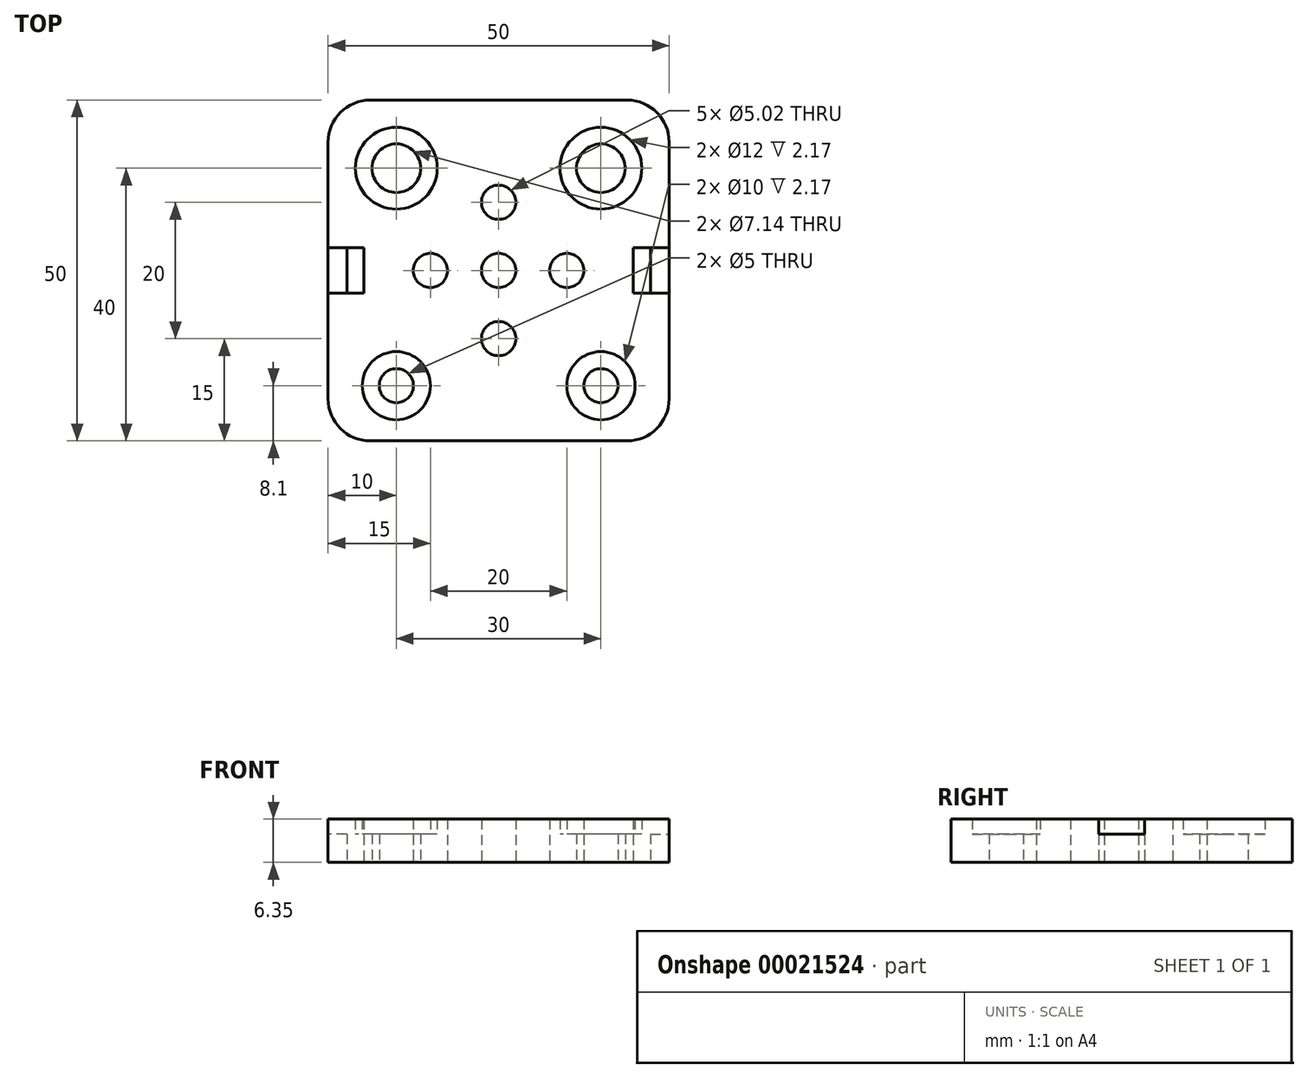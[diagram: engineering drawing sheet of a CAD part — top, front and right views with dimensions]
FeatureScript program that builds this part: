
annotation { "Feature Type Name" : "Feature", "Feature Type Description" : "" }
export const myFeature = defineFeature(function(context is Context, id is Id, definition is map)
    precondition{}
    {
        {
            var Q0;
            Q0=qCreatedBy(makeId("Top.planeOp"),FACE);
            var sketch = newSketch(context, id + "F0", { "sketchPlane" : qUnion([Q0])});
            skLineSegment(sketch, "E0.rect.bottom", {"start": v(18.83, -25) * mm, "end": v(-18.83, -25) * mm});
            skLineSegment(sketch, "E0.rect.top", {"start": v(18.83, 25) * mm, "end": v(-18.83, 25) * mm});
            skLineSegment(sketch, "E0.rect.left", {"start": v(25, -18.83) * mm, "end": v(25, 18.83) * mm});
            skLineSegment(sketch, "E0.rect.right", {"start": v(-25, -18.83) * mm, "end": v(-25, 18.83) * mm});
            skPoint(sketch, "E0.rect.middle", {"position": v(0, 0) * mm});
            skPoint(sketch, "E1.visualSharp", {"position": v(-25, 25) * mm});
            skArc(sketch, "E1.filletArc", {"start": v(-18.83, 25) * mm, "mid": v(-23.2, 23.2) * mm, "end": v(-25, 18.83) * mm});
            skPoint(sketch, "E2.visualSharp", {"position": v(25, 25) * mm});
            skArc(sketch, "E2.filletArc", {"start": v(25, 18.83) * mm, "mid": v(23.2, 23.2) * mm, "end": v(18.83, 25) * mm});
            skPoint(sketch, "E3.visualSharp", {"position": v(25, -25) * mm});
            skArc(sketch, "E3.filletArc", {"start": v(18.83, -25) * mm, "mid": v(23.2, -23.2) * mm, "end": v(25, -18.83) * mm});
            skPoint(sketch, "E4.visualSharp", {"position": v(-25, -25) * mm});
            skArc(sketch, "E4.filletArc", {"start": v(-25, -18.83) * mm, "mid": v(-23.2, -23.2) * mm, "end": v(-18.83, -25) * mm});
            skCircle(sketch, "E5", {"center": v(0, 0) * mm, "radius": 2.5 * mm});
            skCircle(sketch, "E6.1.0.0", {"center": v(10, 0) * mm, "radius": 2.5 * mm});
            skLineSegment(sketch, "E6.direction1", {"start": v(0, 0) * mm, "end": v(10, 0) * mm, "construction": true});
            skCircle(sketch, "E7.1.0.0", {"center": v(-10, 0) * mm, "radius": 2.5 * mm});
            skLineSegment(sketch, "E7.direction1", {"start": v(0, 0) * mm, "end": v(-10, 0) * mm, "construction": true});
            skCircle(sketch, "E8.0.1.0", {"center": v(0, 10) * mm, "radius": 2.5 * mm});
            skLineSegment(sketch, "E8.direction2", {"start": v(0, 0) * mm, "end": v(0, 10) * mm, "construction": true});
            skCircle(sketch, "E9.0.1.0", {"center": v(0, -10) * mm, "radius": 2.5 * mm});
            skLineSegment(sketch, "E9.direction2", {"start": v(0, 0) * mm, "end": v(0, -10) * mm, "construction": true});
            skCircle(sketch, "E10", {"center": v(-15, 15) * mm, "radius": 3.57 * mm});
            skCircle(sketch, "E11", {"center": v(-15, 15) * mm, "radius": 6 * mm});
            skCircle(sketch, "E12.1.0.0", {"center": v(15, 15) * mm, "radius": 6 * mm});
            skCircle(sketch, "E12.1.0.1", {"center": v(15, 15) * mm, "radius": 3.57 * mm});
            skLineSegment(sketch, "E12.direction1", {"start": v(-15, 15) * mm, "end": v(15, 15) * mm, "construction": true});
            skCircle(sketch, "E13", {"center": v(-15, -16.9) * mm, "radius": 2.5 * mm});
            skCircle(sketch, "E14", {"center": v(-15, -16.9) * mm, "radius": 5 * mm});
            skCircle(sketch, "E15.1.0.0", {"center": v(15, -16.9) * mm, "radius": 5 * mm});
            skCircle(sketch, "E15.1.0.1", {"center": v(15, -16.9) * mm, "radius": 2.5 * mm});
            skLineSegment(sketch, "E15.direction1", {"start": v(-15, -16.9) * mm, "end": v(15, -16.9) * mm, "construction": true});
            skLineSegment(sketch, "E16.rect.bottom", {"start": v(-19.75, 3.35) * mm, "end": v(-25, 3.35) * mm});
            skLineSegment(sketch, "E16.rect.top", {"start": v(-19.75, -3.35) * mm, "end": v(-25, -3.35) * mm});
            skLineSegment(sketch, "E16.rect.left", {"start": v(-19.75, 3.35) * mm, "end": v(-19.75, -3.35) * mm});
            skPoint(sketch, "E16.rect.middle", {"position": v(-25, 0) * mm});
            skLineSegment(sketch, "E17", {"start": v(-22.25, 3.35) * mm, "end": v(-22.25, -3.35) * mm});
            skPoint(sketch, "E16.rect.right.start.orphan", {"position": v(-30.25, 3.35) * mm});
            skPoint(sketch, "E18.orphan", {"position": v(-30.25, -3.35) * mm});
            skLineSegment(sketch, "E19.MirrorCS", {"start": v(19.75, 3.35) * mm, "end": v(19.75, -3.35) * mm});
            skLineSegment(sketch, "E20.MirrorCS", {"start": v(22.25, 3.35) * mm, "end": v(22.25, -3.35) * mm});
            skLineSegment(sketch, "E21.MirrorCS", {"start": v(19.75, 3.35) * mm, "end": v(25, 3.35) * mm});
            skLineSegment(sketch, "E22.MirrorCS", {"start": v(19.75, -3.35) * mm, "end": v(25, -3.35) * mm});
            skSolve(sketch);
        }
        {
            var Q0;
            Q0=makeQuery(id+"F0.imprint","IMPRINT",FACE,{"disambiguationData":[TD([[makeQuery(id+"F0.imprint","IMPRINT",EDGE,{"derivedFrom":sQuery(id+"F0.wireOp",EDGE,"E0.rect.bottom")}),-1.0]])]});
            extrude(context, id + "F1", {"entities" : qUnion([Q0]), "depth" : 6.35 * mm});
        }
        {
            var Q0;
            Q0=makeQuery(id+"F0.imprint","IMPRINT",FACE,{"disambiguationData":[TD([[makeQuery(id+"F0.imprint","IMPRINT",EDGE,{"derivedFrom":sQuery(id+"F0.wireOp",EDGE,"E10")}),-1.0]])]});
            var Q1;
            Q1=makeQuery(id+"F0.imprint","IMPRINT",FACE,{"disambiguationData":[TD([[makeQuery(id+"F0.imprint","IMPRINT",EDGE,{"derivedFrom":sQuery(id+"F0.wireOp",EDGE,"E12.1.0.0")}),1.0]])]});
            var Q2;
            Q2=makeQuery(id+"F0.imprint","IMPRINT",FACE,{"disambiguationData":[TD([[makeQuery(id+"F0.imprint","IMPRINT",EDGE,{"derivedFrom":sQuery(id+"F0.wireOp",EDGE,"E13")}),-1.0]])]});
            var Q3;
            Q3=makeQuery(id+"F0.imprint","IMPRINT",FACE,{"disambiguationData":[TD([[makeQuery(id+"F0.imprint","IMPRINT",EDGE,{"derivedFrom":sQuery(id+"F0.wireOp",EDGE,"E15.1.0.0")}),1.0]])]});
            var Q4;
            {var subQ3=sQuery(id+"F0.wireOp",EDGE,"E20.MirrorCS");Q4=makeQuery(id+"F0.imprint","IMPRINT",FACE,{"disambiguationData":[TD([[makeQuery(id+"F0.imprint","IMPRINT",EDGE,{"derivedFrom":subQ3}),1.0]])]});}
            var Q5;
            {var subQ0=sQuery(id+"F0.wireOp",EDGE,"E17");Q5=makeQuery(id+"F0.imprint","IMPRINT",FACE,{"disambiguationData":[TD([[makeQuery(id+"F0.imprint","IMPRINT",EDGE,{"derivedFrom":subQ0}),-1.0]])]});}
            extrude(context, id + "F2", {"entities" : qUnion([Q0, Q1, Q2, Q3, Q4, Q5]), "operationType" : NewBodyOperationType.ADD, "depth" : 4.18 * mm});
        }
    });
